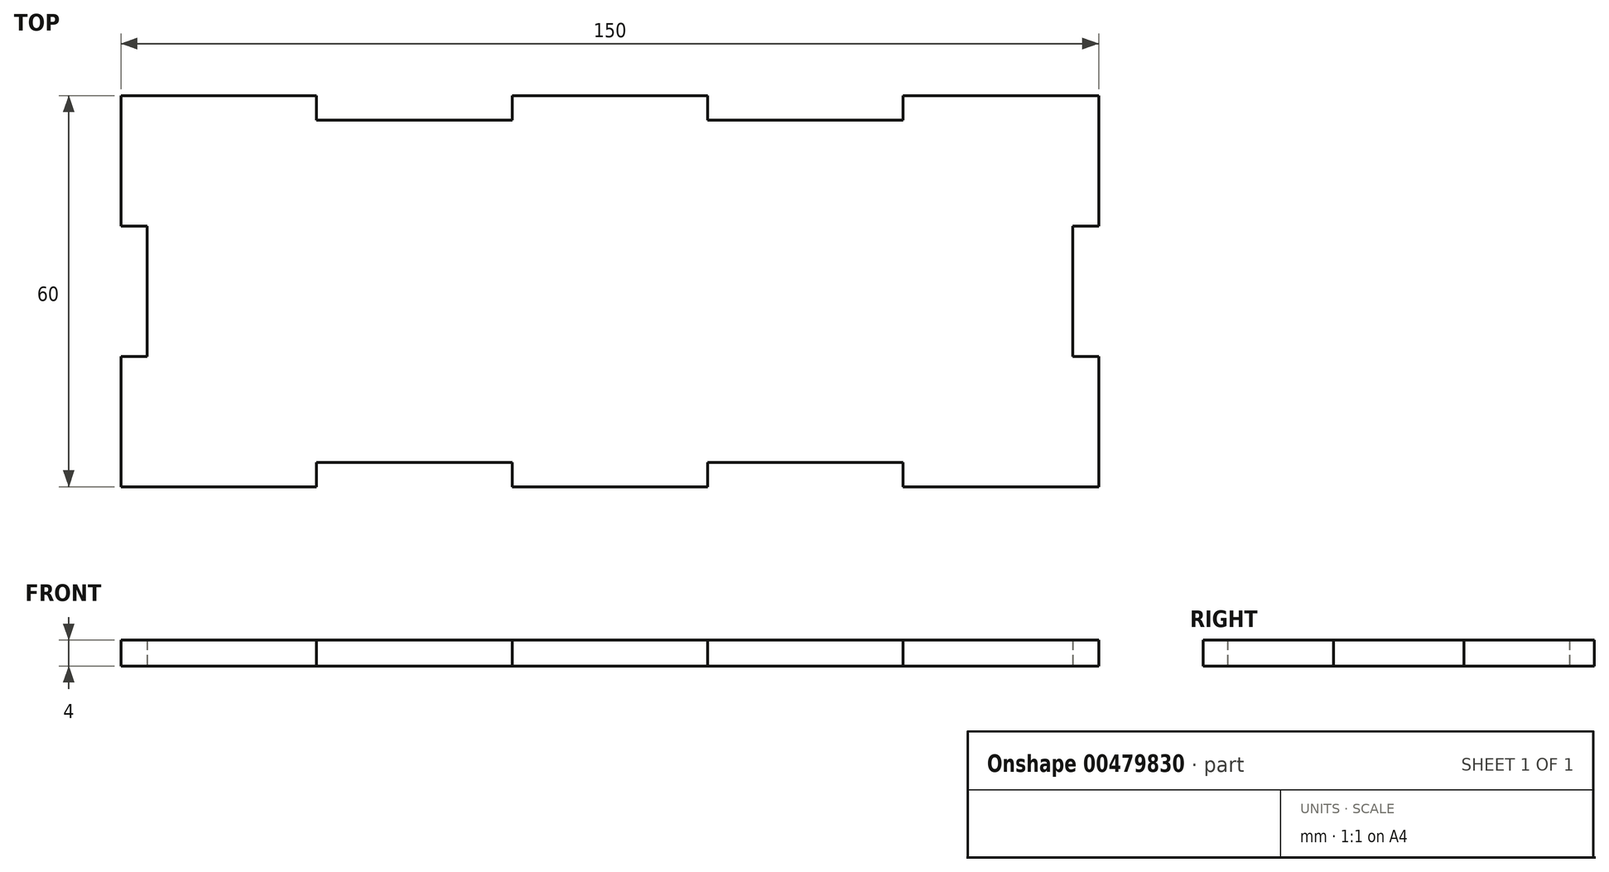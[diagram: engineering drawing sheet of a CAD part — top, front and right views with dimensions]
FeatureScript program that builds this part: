
annotation { "Feature Type Name" : "Feature", "Feature Type Description" : "" }
export const myFeature = defineFeature(function(context is Context, id is Id, definition is map)
    precondition{}
    {
        {
            var Q0;
            Q0=qCreatedBy(makeId("Top.planeOp"),FACE);
            var sketch = newSketch(context, id + "F0", { "sketchPlane" : qUnion([Q0])});
            skLineSegment(sketch, "E0.bottom", {"start": v(0, 0) * mm, "end": v(150, 0) * mm});
            skLineSegment(sketch, "E0.top", {"start": v(0, 60) * mm, "end": v(150, 60) * mm});
            skLineSegment(sketch, "E0.left", {"start": v(0, 0) * mm, "end": v(0, 60) * mm});
            skLineSegment(sketch, "E0.right", {"start": v(150, 0) * mm, "end": v(150, 60) * mm});
            skLineSegment(sketch, "E1.bottom", {"start": v(30, 60) * mm, "end": v(60, 60) * mm});
            skLineSegment(sketch, "E1.top", {"start": v(30, 56.23) * mm, "end": v(60, 56.23) * mm});
            skLineSegment(sketch, "E1.left", {"start": v(30, 60) * mm, "end": v(30, 56.23) * mm});
            skLineSegment(sketch, "E1.right", {"start": v(60, 60) * mm, "end": v(60, 56.23) * mm});
            skLineSegment(sketch, "E2.bottom", {"start": v(30, 0) * mm, "end": v(60, 0) * mm});
            skLineSegment(sketch, "E2.top", {"start": v(30, 3.77) * mm, "end": v(60, 3.77) * mm});
            skLineSegment(sketch, "E2.left", {"start": v(30, 0) * mm, "end": v(30, 3.77) * mm});
            skLineSegment(sketch, "E2.right", {"start": v(60, 0) * mm, "end": v(60, 3.77) * mm});
            skLineSegment(sketch, "E3.bottom", {"start": v(90, 60) * mm, "end": v(120, 60) * mm});
            skLineSegment(sketch, "E3.top", {"start": v(90, 56.23) * mm, "end": v(120, 56.23) * mm});
            skLineSegment(sketch, "E3.left", {"start": v(90, 60) * mm, "end": v(90, 56.23) * mm});
            skLineSegment(sketch, "E3.right", {"start": v(120, 60) * mm, "end": v(120, 56.23) * mm});
            skLineSegment(sketch, "E4.bottom", {"start": v(120, 0) * mm, "end": v(90, 0) * mm});
            skLineSegment(sketch, "E4.top", {"start": v(120, 3.77) * mm, "end": v(90, 3.77) * mm});
            skLineSegment(sketch, "E4.left", {"start": v(120, 0) * mm, "end": v(120, 3.77) * mm});
            skLineSegment(sketch, "E4.right", {"start": v(90, 0) * mm, "end": v(90, 3.77) * mm});
            skLineSegment(sketch, "E5.bottom", {"start": v(0, 40) * mm, "end": v(4, 40) * mm});
            skLineSegment(sketch, "E5.top", {"start": v(0, 20) * mm, "end": v(4, 20) * mm});
            skLineSegment(sketch, "E5.left", {"start": v(0, 40) * mm, "end": v(0, 20) * mm});
            skLineSegment(sketch, "E5.right", {"start": v(4, 40) * mm, "end": v(4, 20) * mm});
            skLineSegment(sketch, "E6.bottom", {"start": v(150, 40) * mm, "end": v(146, 40) * mm});
            skLineSegment(sketch, "E6.top", {"start": v(150, 20) * mm, "end": v(146, 20) * mm});
            skLineSegment(sketch, "E6.left", {"start": v(150, 40) * mm, "end": v(150, 20) * mm});
            skLineSegment(sketch, "E6.right", {"start": v(146, 40) * mm, "end": v(146, 20) * mm});
            skSolve(sketch);
        }
        {
            var Q0;
            Q0=makeQuery(id+"F0.imprint","IMPRINT",FACE,{"disambiguationData":[TD([[makeQuery(id+"F0.imprint","IMPRINT",EDGE,{"derivedFrom":sQuery(id+"F0.wireOp",EDGE,"E1.top")}),-1.0]])]});
            extrude(context, id + "F1", {"entities" : qUnion([Q0]), "depth" : 4 * mm});
        }
    });
